# Revit family: 1Electronics_Community_Biamp_Subwoofer_IS8-215
name_source: partatom
category: Communication Devices
units: mm (PartAtom-declared; Revit-internal decimal feet)

## family parameters
Cut with Voids When Loaded = No
Host = Face
Maintain Annotation Orientation = No
OmniClass Number = 23.85.10.11.14.14.14
OmniClass Title = Loudspeakers
Part Type = Normal
Room Calculation Point = No
Round Connector Dimension = Use Diameter
Shared = No

## types (2) — shared parameters
Continuous Power Handling  Nominal Impedance = Single Amp - 89V, 2000W @ 4 ohms (8000W peak); Dual Amp - 89V, 1000W @ 8 ohms (4000W peak) (each);
Default Elevation = 48 "
Depth = 23.35 "
Description = IS8-215 High Power Dual 15-Inch Subwoofer
Environmental = Outdoor: IP55W per IEC 60529, MIL-STD-810G
Equalized Maximum SPL = Half Space - Peak: 139 dB - Continuous: 133 dB; Whole Space - Peak: 133 dB - Continuous: 127 dB
Equalized Sensitivity = Half Space - 1W: 100 dB - 2.83V: 103 dB; Whole Space - 1W: 94 dB - 2.83V: 97 dB
Height = 39 "
Input Connection = Screw terminal blocks (4-position)
Manufacturer = Biamp
Mounting Points = (24) M10 threaded rigging points
Nominal Maximum SPL = Half Space - Peak: 141 dB - Continuous: 135 dB; Whole Space - Peak: 135 dB - Continuous: 129 dB
Nominal Sensitivity = Half Space - 1W: 102 dB - 2.83V: 105 dB; Whole Space - 1W: 96 dB - 2.83V: 99 dB
Operating Environment = Indoor
Operating Mode = Single or Dual Amp
Operating Range = 36 Hz to 140 Hz
Product Documentation Link = https://downloads.biamp.com
Product Page URL = https://www.biamp.com
Product data url = https://bimobject.com
Recommended Amplifiers = Single Amp - 2000W - 4000W @ 4 ohms,  (89V - 126V); Dual Amp - 1000W - 2000W @ 8 ohms,  (89V - 126V) (each driver)
Shipping Weight = 135.00 lbf
Transducers = 2 x 15 (381mm) double-treated cones with 4 (102mm) voice coils, demodulation rings, neodymium construction
URL = https://www.biamp.com
Weight = 114.00 lbf
Width = 16.5 "

## per-type parameters (varying)
| type | Grill Material | Housing Material |
| IS8-215 B | Biamp - Plastic - Black(Grid) | Biamp - Plastic - Black |
| IS8-215 W | Biamp - Plastic - White(Grid) | Biamp - Plastic - White |

note: column(s) folded — value = type name in every type: Model

## geometry (parser evidence)
native form markers: Sweep x1
no freeform markers — native parametric forms only
